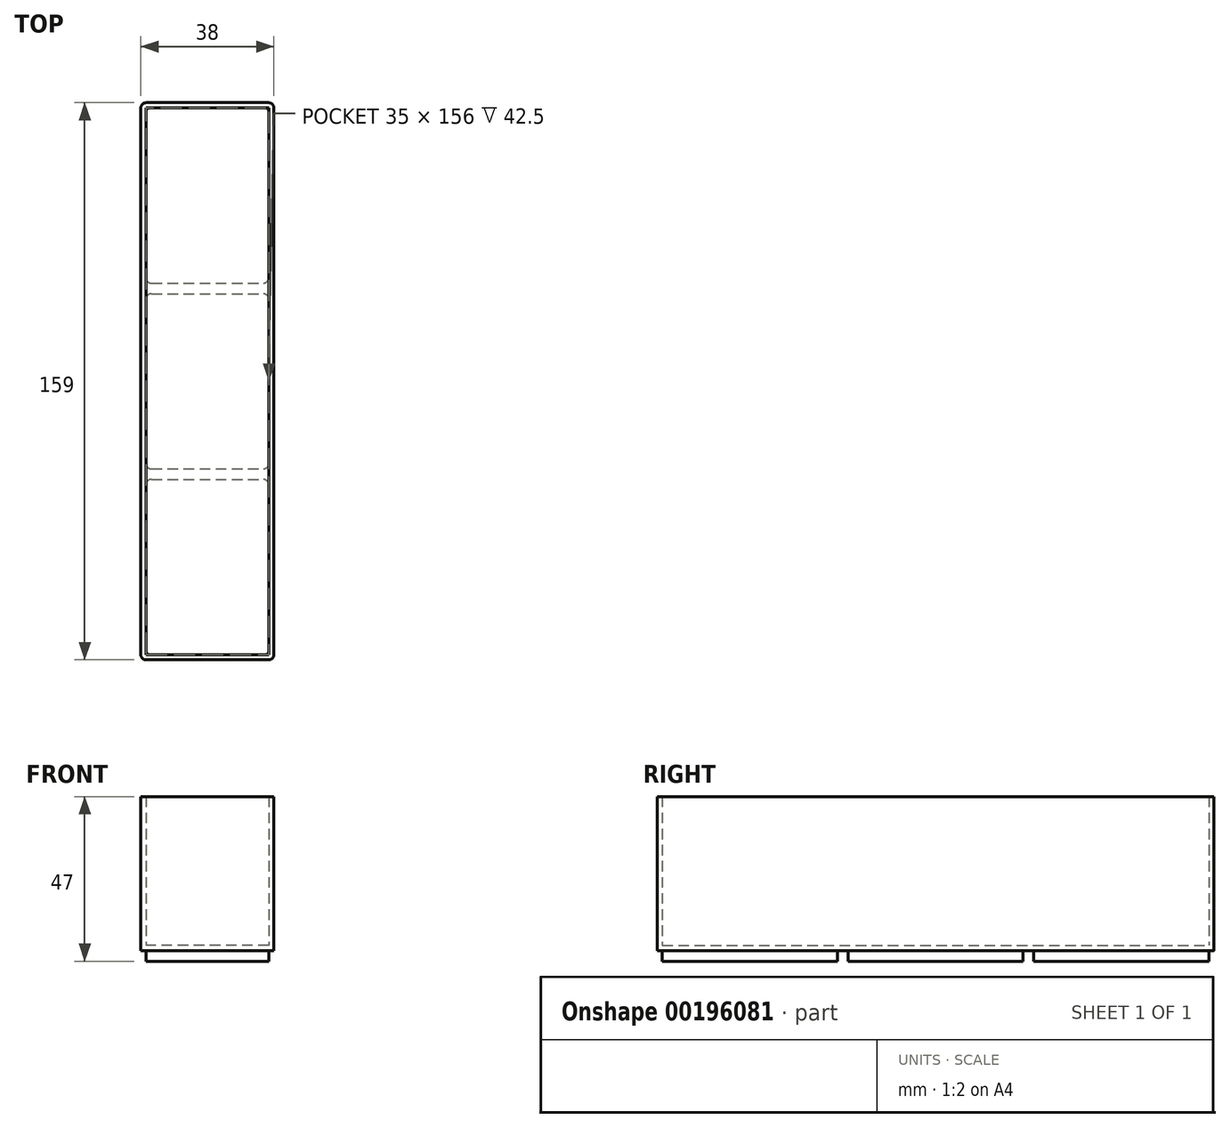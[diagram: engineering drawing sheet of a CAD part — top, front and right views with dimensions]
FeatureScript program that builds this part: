
annotation { "Feature Type Name" : "Feature", "Feature Type Description" : "" }
export const myFeature = defineFeature(function(context is Context, id is Id, definition is map)
    precondition{}
    {
        {
            var Q0;
            Q0=qCreatedBy(makeId("Top.planeOp"),FACE);
            var sketch = newSketch(context, id + "F0", { "sketchPlane" : qUnion([Q0])});
            skLineSegment(sketch, "E0.bottom", {"start": v(0, 0) * mm, "end": v(38, 0) * mm});
            skLineSegment(sketch, "E0.top", {"start": v(0, 53) * mm, "end": v(38, 53) * mm});
            skLineSegment(sketch, "E0.left", {"start": v(0, 0) * mm, "end": v(0, 53) * mm});
            skLineSegment(sketch, "E0.right", {"start": v(38, 0) * mm, "end": v(38, 53) * mm});
            skLineSegment(sketch, "E1.bottom", {"start": v(1.5, 1.5) * mm, "end": v(36.5, 1.5) * mm});
            skLineSegment(sketch, "E1.top", {"start": v(1.5, 51.5) * mm, "end": v(36.5, 51.5) * mm});
            skLineSegment(sketch, "E1.left", {"start": v(1.5, 1.5) * mm, "end": v(1.5, 51.5) * mm});
            skLineSegment(sketch, "E1.right", {"start": v(36.5, 1.5) * mm, "end": v(36.5, 51.5) * mm});
            skLineSegment(sketch, "E2.top", {"start": v(0, 106) * mm, "end": v(38, 106) * mm});
            skLineSegment(sketch, "E2.left", {"start": v(0, 53) * mm, "end": v(0, 106) * mm});
            skLineSegment(sketch, "E2.right", {"start": v(38, 53) * mm, "end": v(38, 106) * mm});
            skLineSegment(sketch, "E3.bottom", {"start": v(1.5, 54.5) * mm, "end": v(36.5, 54.5) * mm});
            skLineSegment(sketch, "E3.top", {"start": v(1.5, 104.5) * mm, "end": v(36.5, 104.5) * mm});
            skLineSegment(sketch, "E3.left", {"start": v(1.5, 54.5) * mm, "end": v(1.5, 104.5) * mm});
            skLineSegment(sketch, "E3.right", {"start": v(36.5, 54.5) * mm, "end": v(36.5, 104.5) * mm});
            skLineSegment(sketch, "E4.top", {"start": v(0, 159) * mm, "end": v(38, 159) * mm});
            skLineSegment(sketch, "E4.left", {"start": v(0, 106) * mm, "end": v(0, 159) * mm});
            skLineSegment(sketch, "E4.right", {"start": v(38, 106) * mm, "end": v(38, 159) * mm});
            skLineSegment(sketch, "E5.bottom", {"start": v(1.5, 107.5) * mm, "end": v(36.5, 107.5) * mm});
            skLineSegment(sketch, "E5.top", {"start": v(1.5, 157.5) * mm, "end": v(36.5, 157.5) * mm});
            skLineSegment(sketch, "E5.left", {"start": v(1.5, 107.5) * mm, "end": v(1.5, 157.5) * mm});
            skLineSegment(sketch, "E5.right", {"start": v(36.5, 107.5) * mm, "end": v(36.5, 157.5) * mm});
            skLineSegment(sketch, "E6", {"start": v(1.5, 107.5) * mm, "end": v(1.5, 104.5) * mm});
            skLineSegment(sketch, "E7", {"start": v(36.5, 107.5) * mm, "end": v(36.5, 104.5) * mm});
            skLineSegment(sketch, "E8", {"start": v(36.5, 54.5) * mm, "end": v(36.5, 51.5) * mm});
            skLineSegment(sketch, "E9", {"start": v(1.5, 54.5) * mm, "end": v(1.5, 51.5) * mm});
            skSolve(sketch);
        }
        {
            var Q0;
            Q0=makeQuery(id+"F0.imprint","IMPRINT",FACE,{"disambiguationData":[TD([[makeQuery(id+"F0.imprint","IMPRINT",EDGE,{"derivedFrom":sQuery(id+"F0.wireOp",EDGE,"E5.bottom")}),1.0]])]});
            var Q1;
            Q1=makeQuery(id+"F0.imprint","IMPRINT",FACE,{"disambiguationData":[TD([[makeQuery(id+"F0.imprint","IMPRINT",EDGE,{"derivedFrom":sQuery(id+"F0.wireOp",EDGE,"E3.bottom")}),1.0]])]});
            var Q2;
            Q2=makeQuery(id+"F0.imprint","IMPRINT",FACE,{"disambiguationData":[TD([[makeQuery(id+"F0.imprint","IMPRINT",EDGE,{"derivedFrom":sQuery(id+"F0.wireOp",EDGE,"E1.bottom")}),1.0]])]});
            extrude(context, id + "F1", {"entities" : qUnion([Q0, Q1, Q2]), "oppositeDirection" : true, "depth" : 3 * mm, "offsetDistance" : 25 * mm});
        }
        {
            var Q0;
            Q0=makeQuery(id+"F0.imprint","IMPRINT",FACE,{"disambiguationData":[TD([[makeQuery(id+"F0.imprint","IMPRINT",EDGE,{"derivedFrom":sQuery(id+"F0.wireOp",EDGE,"E4.top")}),-1.0]])]});
            var Q1;
            Q1=makeQuery(id+"F0.imprint","IMPRINT",FACE,{"disambiguationData":[TD([[makeQuery(id+"F0.imprint","IMPRINT",EDGE,{"derivedFrom":sQuery(id+"F0.wireOp",EDGE,"E5.bottom")}),1.0]])]});
            var Q2;
            {var subQ0=sQuery(id+"F0.wireOp",EDGE,"E3.top");Q2=makeQuery(id+"F0.imprint","IMPRINT",FACE,{"disambiguationData":[TD([[makeQuery(id+"F0.imprint","IMPRINT",EDGE,{"derivedFrom":subQ0}),1.0]])]});}
            var Q3;
            {var subQ5=sQuery(id+"F0.wireOp",EDGE,"E5.bottom");Q3=makeQuery(id+"F0.imprint","IMPRINT",FACE,{"disambiguationData":[TD([[makeQuery(id+"F0.imprint","IMPRINT",EDGE,{"derivedFrom":subQ5}),-1.0]])]});}
            var Q4;
            {var subQ1=sQuery(id+"F0.wireOp",EDGE,"E2.right");Q4=makeQuery(id+"F0.imprint","IMPRINT",FACE,{"disambiguationData":[TD([[makeQuery(id+"F0.imprint","IMPRINT",EDGE,{"derivedFrom":subQ1}),1.0]])]});}
            var Q5;
            {var subQ1=sQuery(id+"F0.wireOp",EDGE,"E2.left");Q5=makeQuery(id+"F0.imprint","IMPRINT",FACE,{"disambiguationData":[TD([[makeQuery(id+"F0.imprint","IMPRINT",EDGE,{"derivedFrom":subQ1}),-1.0]])]});}
            var Q6;
            Q6=makeQuery(id+"F0.imprint","IMPRINT",FACE,{"disambiguationData":[TD([[makeQuery(id+"F0.imprint","IMPRINT",EDGE,{"derivedFrom":sQuery(id+"F0.wireOp",EDGE,"E3.bottom")}),1.0]])]});
            var Q7;
            {var subQ5=sQuery(id+"F0.wireOp",EDGE,"E3.bottom");Q7=makeQuery(id+"F0.imprint","IMPRINT",FACE,{"disambiguationData":[TD([[makeQuery(id+"F0.imprint","IMPRINT",EDGE,{"derivedFrom":subQ5}),-1.0]])]});}
            var Q8;
            {var subQ0=sQuery(id+"F0.wireOp",EDGE,"E1.top");Q8=makeQuery(id+"F0.imprint","IMPRINT",FACE,{"disambiguationData":[TD([[makeQuery(id+"F0.imprint","IMPRINT",EDGE,{"derivedFrom":subQ0}),1.0]])]});}
            var Q9;
            Q9=makeQuery(id+"F0.imprint","IMPRINT",FACE,{"disambiguationData":[TD([[makeQuery(id+"F0.imprint","IMPRINT",EDGE,{"derivedFrom":sQuery(id+"F0.wireOp",EDGE,"E1.bottom")}),1.0]])]});
            var Q10;
            Q10=makeQuery(id+"F0.imprint","IMPRINT",FACE,{"disambiguationData":[TD([[makeQuery(id+"F0.imprint","IMPRINT",EDGE,{"derivedFrom":sQuery(id+"F0.wireOp",EDGE,"E0.bottom")}),1.0]])]});
            extrude(context, id + "F2", {"entities" : qUnion([Q0, Q1, Q2, Q3, Q4, Q5, Q6, Q7, Q8, Q9, Q10]), "operationType" : NewBodyOperationType.ADD, "depth" : 1.5 * mm, "offsetDistance" : 25 * mm});
        }
        {
            var Q0;
            Q0=makeQuery(id+"F0.imprint","IMPRINT",FACE,{"disambiguationData":[TD([[makeQuery(id+"F0.imprint","IMPRINT",EDGE,{"derivedFrom":sQuery(id+"F0.wireOp",EDGE,"E4.top")}),-1.0]])]});
            var Q1;
            {var subQ1=sQuery(id+"F0.wireOp",EDGE,"E2.left");Q1=makeQuery(id+"F0.imprint","IMPRINT",FACE,{"disambiguationData":[TD([[makeQuery(id+"F0.imprint","IMPRINT",EDGE,{"derivedFrom":subQ1}),-1.0]])]});}
            var Q2;
            {var subQ1=sQuery(id+"F0.wireOp",EDGE,"E2.right");Q2=makeQuery(id+"F0.imprint","IMPRINT",FACE,{"disambiguationData":[TD([[makeQuery(id+"F0.imprint","IMPRINT",EDGE,{"derivedFrom":subQ1}),1.0]])]});}
            var Q3;
            Q3=makeQuery(id+"F0.imprint","IMPRINT",FACE,{"disambiguationData":[TD([[makeQuery(id+"F0.imprint","IMPRINT",EDGE,{"derivedFrom":sQuery(id+"F0.wireOp",EDGE,"E0.bottom")}),1.0]])]});
            extrude(context, id + "F3", {"entities" : qUnion([Q0, Q1, Q2, Q3]), "operationType" : NewBodyOperationType.ADD, "depth" : 44 * mm, "offsetDistance" : 25 * mm});
        }
        {
            var Q0;
            {var subQ0=sQuery(id+"F0.wireOp",EDGE,"E4.left");var subQ1=sQuery(id+"F0.wireOp",EDGE,"E4.top");Q0=makeQuery(id+"F3.boolean.opBoolean","MERGE",EDGE,{"derivedFrom":[makeQuery(id+"F2.opExtrude","SWEPT_EDGE",EDGE,{"disambiguationData":[OSD([subQ1,subQ0])]}),makeQuery(id+"F3.opExtrude","SWEPT_EDGE",EDGE,{"disambiguationData":[OSD([subQ1,subQ0])]})]});}
            var Q1;
            {var subQ0=sQuery(id+"F0.wireOp",EDGE,"E4.right");var subQ1=sQuery(id+"F0.wireOp",EDGE,"E4.top");Q1=makeQuery(id+"F3.boolean.opBoolean","MERGE",EDGE,{"derivedFrom":[makeQuery(id+"F2.opExtrude","SWEPT_EDGE",EDGE,{"disambiguationData":[OSD([subQ1,subQ0])]}),makeQuery(id+"F3.opExtrude","SWEPT_EDGE",EDGE,{"disambiguationData":[OSD([subQ1,subQ0])]})]});}
            var Q2;
            Q2=makeQuery(id+"F1.opExtrude","SWEPT_EDGE",EDGE,{"disambiguationData":[OSD([sQuery(id+"F0.wireOp",EDGE,"E5.top"),sQuery(id+"F0.wireOp",EDGE,"E5.right")])]});
            var Q3;
            Q3=makeQuery(id+"F1.opExtrude","SWEPT_EDGE",EDGE,{"disambiguationData":[OSD([sQuery(id+"F0.wireOp",EDGE,"E5.top"),sQuery(id+"F0.wireOp",EDGE,"E5.left")])]});
            var Q4;
            Q4=makeQuery(id+"F1.opExtrude","SWEPT_EDGE",EDGE,{"disambiguationData":[OSD([sQuery(id+"F0.wireOp",EDGE,"E5.bottom"),sQuery(id+"F0.wireOp",EDGE,"E5.right"),sQuery(id+"F0.wireOp",EDGE,"E7")])]});
            var Q5;
            Q5=makeQuery(id+"F1.opExtrude","SWEPT_EDGE",EDGE,{"disambiguationData":[OSD([sQuery(id+"F0.wireOp",EDGE,"E5.bottom"),sQuery(id+"F0.wireOp",EDGE,"E5.left"),sQuery(id+"F0.wireOp",EDGE,"E6")])]});
            var Q6;
            Q6=makeQuery(id+"F1.opExtrude","SWEPT_EDGE",EDGE,{"disambiguationData":[OSD([sQuery(id+"F0.wireOp",EDGE,"E3.top"),sQuery(id+"F0.wireOp",EDGE,"E3.left"),sQuery(id+"F0.wireOp",EDGE,"E6")])]});
            var Q7;
            Q7=makeQuery(id+"F1.opExtrude","SWEPT_EDGE",EDGE,{"disambiguationData":[OSD([sQuery(id+"F0.wireOp",EDGE,"E3.top"),sQuery(id+"F0.wireOp",EDGE,"E3.right"),sQuery(id+"F0.wireOp",EDGE,"E7")])]});
            var Q8;
            Q8=makeQuery(id+"F1.opExtrude","SWEPT_EDGE",EDGE,{"disambiguationData":[OSD([sQuery(id+"F0.wireOp",EDGE,"E3.bottom"),sQuery(id+"F0.wireOp",EDGE,"E3.right"),sQuery(id+"F0.wireOp",EDGE,"E8")])]});
            var Q9;
            Q9=makeQuery(id+"F1.opExtrude","SWEPT_EDGE",EDGE,{"disambiguationData":[OSD([sQuery(id+"F0.wireOp",EDGE,"E1.top"),sQuery(id+"F0.wireOp",EDGE,"E1.right"),sQuery(id+"F0.wireOp",EDGE,"E8")])]});
            var Q10;
            Q10=makeQuery(id+"F1.opExtrude","SWEPT_EDGE",EDGE,{"disambiguationData":[OSD([sQuery(id+"F0.wireOp",EDGE,"E1.top"),sQuery(id+"F0.wireOp",EDGE,"E1.left"),sQuery(id+"F0.wireOp",EDGE,"E9")])]});
            var Q11;
            Q11=makeQuery(id+"F1.opExtrude","SWEPT_EDGE",EDGE,{"disambiguationData":[OSD([sQuery(id+"F0.wireOp",EDGE,"E3.bottom"),sQuery(id+"F0.wireOp",EDGE,"E3.left"),sQuery(id+"F0.wireOp",EDGE,"E9")])]});
            var Q12;
            Q12=makeQuery(id+"F1.opExtrude","SWEPT_EDGE",EDGE,{"disambiguationData":[OSD([sQuery(id+"F0.wireOp",EDGE,"E1.bottom"),sQuery(id+"F0.wireOp",EDGE,"E1.right")])]});
            var Q13;
            {var subQ0=sQuery(id+"F0.wireOp",EDGE,"E0.right");var subQ1=sQuery(id+"F0.wireOp",EDGE,"E0.bottom");Q13=makeQuery(id+"F3.boolean.opBoolean","MERGE",EDGE,{"derivedFrom":[makeQuery(id+"F2.opExtrude","SWEPT_EDGE",EDGE,{"disambiguationData":[OSD([subQ1,subQ0])]}),makeQuery(id+"F3.opExtrude","SWEPT_EDGE",EDGE,{"disambiguationData":[OSD([subQ1,subQ0])]})]});}
            var Q14;
            Q14=makeQuery(id+"F1.opExtrude","SWEPT_EDGE",EDGE,{"disambiguationData":[OSD([sQuery(id+"F0.wireOp",EDGE,"E1.bottom"),sQuery(id+"F0.wireOp",EDGE,"E1.left")])]});
            var Q15;
            {var subQ0=sQuery(id+"F0.wireOp",EDGE,"E0.left");var subQ1=sQuery(id+"F0.wireOp",EDGE,"E0.bottom");Q15=makeQuery(id+"F3.boolean.opBoolean","MERGE",EDGE,{"derivedFrom":[makeQuery(id+"F2.opExtrude","SWEPT_EDGE",EDGE,{"disambiguationData":[OSD([subQ1,subQ0])]}),makeQuery(id+"F3.opExtrude","SWEPT_EDGE",EDGE,{"disambiguationData":[OSD([subQ1,subQ0])]})]});}
            fillet(context, id + "F4", {"entities" : qUnion([Q0, Q1, Q2, Q3, Q4, Q5, Q6, Q7, Q8, Q9, Q10, Q11, Q12, Q13, Q14, Q15]), "radius" : 1.5 * mm, "tangentPropagation" : true, "allowEdgeOverflow" : false});
        }
    });
